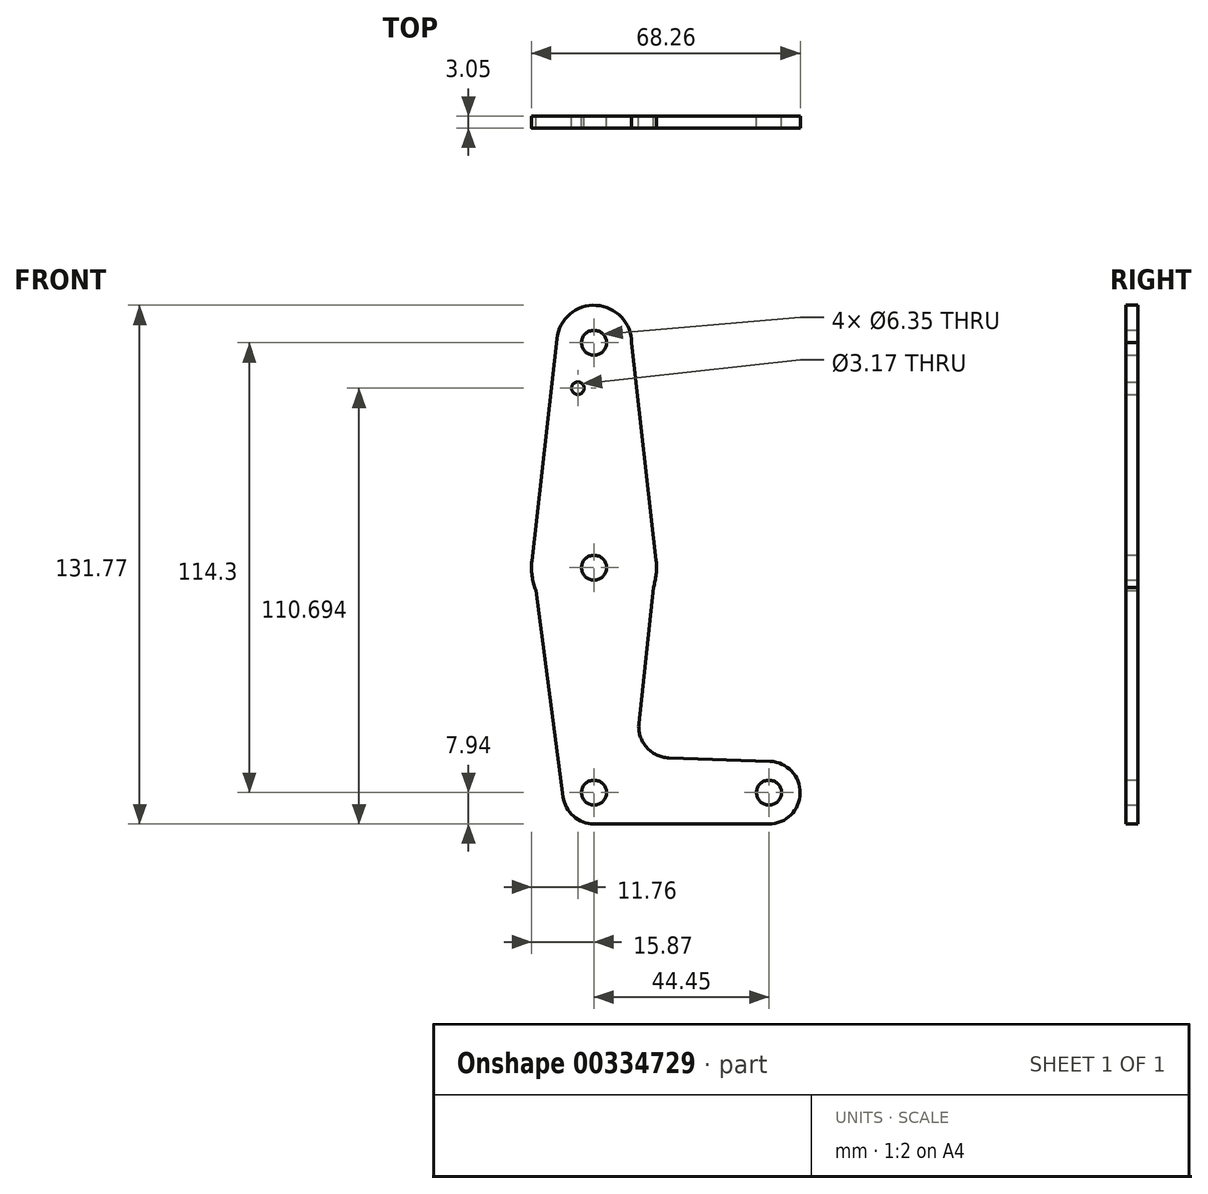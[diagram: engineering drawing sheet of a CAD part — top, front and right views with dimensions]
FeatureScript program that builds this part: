
annotation { "Feature Type Name" : "Feature", "Feature Type Description" : "" }
export const myFeature = defineFeature(function(context is Context, id is Id, definition is map)
    precondition{}
    {
        {
            var Q0;
            Q0=qCreatedBy(makeId("Front.planeOp"),FACE);
            var sketch = newSketch(context, id + "F0", { "sketchPlane" : qUnion([Q0])});
            skLineSegment(sketch, "E0", {"start": v(0, 0) * mm, "end": v(0, 114.3) * mm, "construction": true});
            skCircle(sketch, "E1", {"center": v(0, 114.3) * mm, "radius": 9.53 * mm});
            skCircle(sketch, "E2", {"center": v(0, 57.15) * mm, "radius": 15.88 * mm});
            skLineSegment(sketch, "E3", {"start": v(0, 0) * mm, "end": v(44.45, 0) * mm});
            skCircle(sketch, "E4", {"center": v(44.45, 0) * mm, "radius": 7.94 * mm});
            skLineSegment(sketch, "E5", {"start": v(9.52, 114.3) * mm, "end": v(15.77, 58.93) * mm});
            skLineSegment(sketch, "E6", {"start": v(-9.47, 115.36) * mm, "end": v(-15.78, 58.91) * mm});
            skLineSegment(sketch, "E7", {"start": v(-15.78, 58.91) * mm, "end": v(-15.78, 58.91) * mm});
            skCircle(sketch, "E8", {"center": v(0, 114.3) * mm, "radius": 3.18 * mm});
            skCircle(sketch, "E9", {"center": v(0, 57.15) * mm, "radius": 3.18 * mm});
            skCircle(sketch, "E10", {"center": v(0, 0) * mm, "radius": 3.18 * mm});
            skCircle(sketch, "E11", {"center": v(44.45, 0) * mm, "radius": 3.18 * mm});
            skCircle(sketch, "E12", {"center": v(-4.1, 102.75) * mm, "radius": 1.59 * mm});
            skCircle(sketch, "E13", {"center": v(0, 0) * mm, "radius": 7.94 * mm});
            skLineSegment(sketch, "E14", {"start": v(-15.78, 58.91) * mm, "end": v(-14.78, 51.36) * mm});
            skLineSegment(sketch, "E15", {"start": v(0, -7.94) * mm, "end": v(44.45, -7.94) * mm});
            skLineSegment(sketch, "E16", {"start": v(15.77, 58.93) * mm, "end": v(11.4, 17.63) * mm});
            skLineSegment(sketch, "E17", {"start": v(19.02, 8.85) * mm, "end": v(44.73, 7.93) * mm});
            skPoint(sketch, "E18.orphan", {"position": v(-8, 0) * mm});
            skLineSegment(sketch, "E19", {"start": v(-15.78, 58.91) * mm, "end": v(-8, 0) * mm});
            skLineSegment(sketch, "E20", {"start": v(-8, 0) * mm, "end": v(-7.87, -1.04) * mm});
            skArc(sketch, "E21.filletArc", {"start": v(11.4, 17.63) * mm, "mid": v(13.3, 11.58) * mm, "end": v(19.02, 8.85) * mm});
            skSolve(sketch);
        }
        {
            var Q0;
            Q0 = qSketchRegion(id + "F0", true);
            extrude(context, id + "F1", {"entities" : qUnion([Q0]), "depth" : 3.05 * mm});
        }
    });
